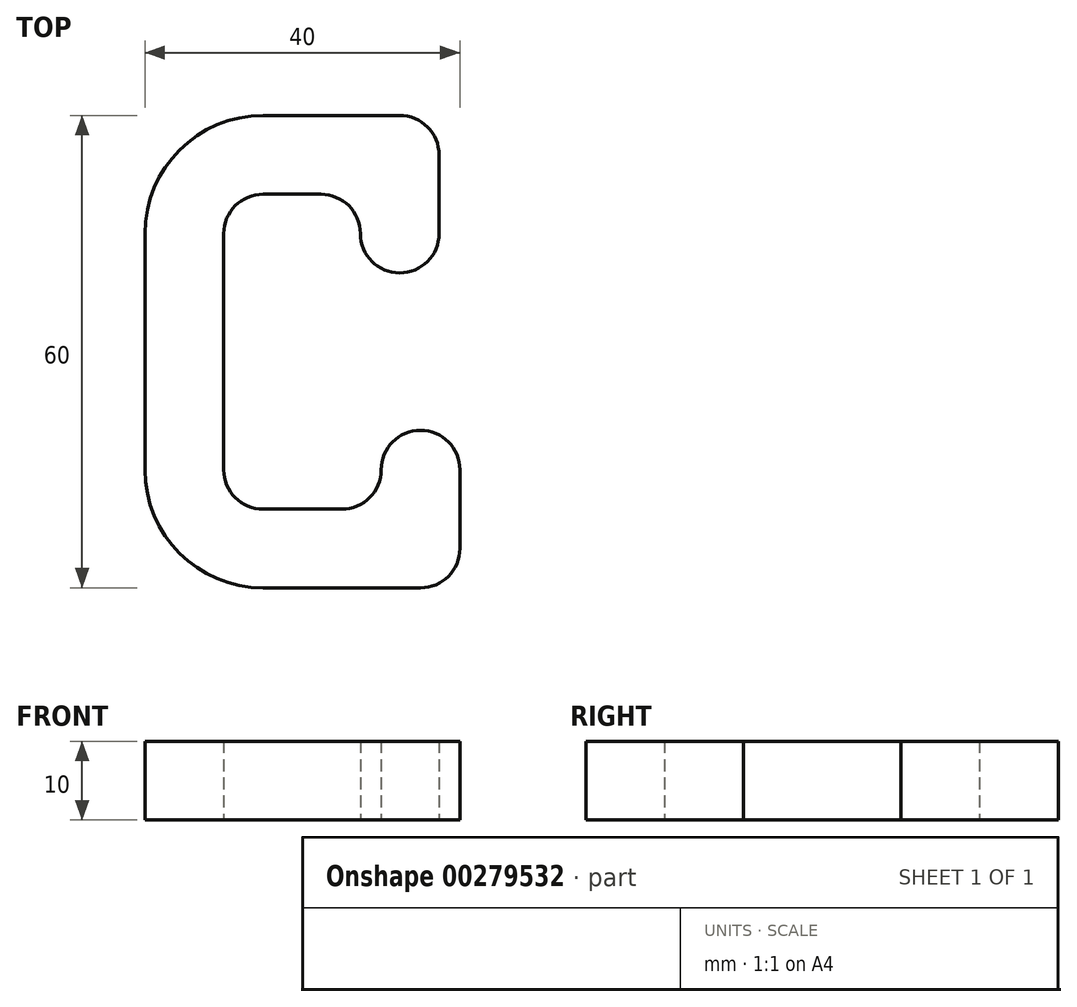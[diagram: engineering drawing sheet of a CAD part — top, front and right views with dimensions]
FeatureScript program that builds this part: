
annotation { "Feature Type Name" : "Feature", "Feature Type Description" : "" }
export const myFeature = defineFeature(function(context is Context, id is Id, definition is map)
    precondition{}
    {
        {
            var Q0;
            Q0=qCreatedBy(makeId("Top.planeOp"),FACE);
            var sketch = newSketch(context, id + "F0", { "sketchPlane" : qUnion([Q0])});
            skLineSegment(sketch, "E0.bottom", {"start": v(-16.46, 31.59) * mm, "end": v(-6.46, 31.59) * mm});
            skLineSegment(sketch, "E0.top", {"start": v(-16.46, -18.41) * mm, "end": v(-6.46, -18.41) * mm});
            skLineSegment(sketch, "E0.left", {"start": v(-16.46, 31.59) * mm, "end": v(-16.46, -18.41) * mm});
            skLineSegment(sketch, "E0.right", {"start": v(-6.46, 31.59) * mm, "end": v(-6.46, -18.41) * mm});
            skLineSegment(sketch, "E1.bottom", {"start": v(-16.46, 41.59) * mm, "end": v(10.9, 41.59) * mm});
            skLineSegment(sketch, "E1.top", {"start": v(-16.46, 31.59) * mm, "end": v(10.9, 31.59) * mm});
            skLineSegment(sketch, "E1.left", {"start": v(-16.46, 41.59) * mm, "end": v(-16.46, 31.59) * mm});
            skLineSegment(sketch, "E1.right", {"start": v(10.9, 41.59) * mm, "end": v(10.9, 31.59) * mm});
            skLineSegment(sketch, "E2.bottom", {"start": v(10.9, 41.59) * mm, "end": v(20.9, 41.59) * mm});
            skLineSegment(sketch, "E2.top", {"start": v(10.9, 21.59) * mm, "end": v(20.9, 21.59) * mm});
            skLineSegment(sketch, "E2.left", {"start": v(10.9, 41.59) * mm, "end": v(10.9, 21.59) * mm});
            skLineSegment(sketch, "E2.right", {"start": v(20.9, 41.59) * mm, "end": v(20.9, 21.59) * mm});
            skLineSegment(sketch, "E3.bottom", {"start": v(13.54, 1.59) * mm, "end": v(23.54, 1.59) * mm});
            skLineSegment(sketch, "E3.top", {"start": v(13.54, -8.41) * mm, "end": v(23.54, -8.41) * mm});
            skLineSegment(sketch, "E3.left", {"start": v(13.54, 1.59) * mm, "end": v(13.54, -8.41) * mm});
            skLineSegment(sketch, "E3.right", {"start": v(23.54, 1.59) * mm, "end": v(23.54, -8.41) * mm});
            skLineSegment(sketch, "E4.bottom", {"start": v(-6.46, -8.41) * mm, "end": v(23.54, -8.41) * mm});
            skLineSegment(sketch, "E4.top", {"start": v(-6.46, -18.41) * mm, "end": v(23.54, -18.41) * mm});
            skLineSegment(sketch, "E4.left", {"start": v(-6.46, -8.41) * mm, "end": v(-6.46, -18.41) * mm});
            skLineSegment(sketch, "E4.right", {"start": v(23.54, -8.41) * mm, "end": v(23.54, -18.41) * mm});
            skSolve(sketch);
        }
        {
            var Q0;
            {var subQ3=sQuery(id+"F0.wireOp",EDGE,"E2.bottom");Q0=makeQuery(id+"F0.imprint","IMPRINT",FACE,{"disambiguationData":[TD([[makeQuery(id+"F0.imprint","IMPRINT",EDGE,{"derivedFrom":subQ3}),-1.0]])]});}
            var Q1;
            {var subQ5=sQuery(id+"F0.wireOp",EDGE,"E1.bottom");Q1=makeQuery(id+"F0.imprint","IMPRINT",FACE,{"disambiguationData":[TD([[makeQuery(id+"F0.imprint","IMPRINT",EDGE,{"derivedFrom":subQ5}),-1.0]])]});}
            var Q2;
            Q2=makeQuery(id+"F0.imprint","IMPRINT",FACE,{"disambiguationData":[TD([[makeQuery(id+"F0.imprint","IMPRINT",EDGE,{"derivedFrom":sQuery(id+"F0.wireOp",EDGE,"E0.top")}),1.0]])]});
            var Q3;
            Q3=makeQuery(id+"F0.imprint","IMPRINT",FACE,{"disambiguationData":[TD([[makeQuery(id+"F0.imprint","IMPRINT",EDGE,{"derivedFrom":sQuery(id+"F0.wireOp",EDGE,"E4.top")}),1.0]])]});
            var Q4;
            Q4=makeQuery(id+"F0.imprint","IMPRINT",FACE,{"disambiguationData":[TD([[makeQuery(id+"F0.imprint","IMPRINT",EDGE,{"derivedFrom":sQuery(id+"F0.wireOp",EDGE,"E3.bottom")}),-1.0]])]});
            extrude(context, id + "F1", {"entities" : qUnion([Q0, Q1, Q2, Q3, Q4]), "depth" : 10 * mm});
        }
        {
            var Q0;
            Q0=makeQuery(id+"F1.opExtrude","SWEPT_EDGE",EDGE,{"disambiguationData":[OSD([sQuery(id+"F0.wireOp",EDGE,"E3.bottom"),sQuery(id+"F0.wireOp",EDGE,"E3.left")])]});
            var Q1;
            Q1=makeQuery(id+"F1.opExtrude","SWEPT_EDGE",EDGE,{"disambiguationData":[OSD([sQuery(id+"F0.wireOp",EDGE,"E2.top"),sQuery(id+"F0.wireOp",EDGE,"E2.left")])]});
            var Q2;
            Q2=makeQuery(id+"F1.opExtrude","SWEPT_EDGE",EDGE,{"disambiguationData":[OSD([sQuery(id+"F0.wireOp",EDGE,"E1.top"),sQuery(id+"F0.wireOp",EDGE,"E2.left")])]});
            var Q3;
            Q3=makeQuery(id+"F1.opExtrude","SWEPT_EDGE",EDGE,{"disambiguationData":[OSD([sQuery(id+"F0.wireOp",EDGE,"E0.right"),sQuery(id+"F0.wireOp",EDGE,"E1.top")])]});
            var Q4;
            Q4=makeQuery(id+"F1.opExtrude","SWEPT_EDGE",EDGE,{"disambiguationData":[OSD([sQuery(id+"F0.wireOp",EDGE,"E0.right"),sQuery(id+"F0.wireOp",EDGE,"E4.bottom"),sQuery(id+"F0.wireOp",EDGE,"E4.left")])]});
            var Q5;
            Q5=makeQuery(id+"F1.opExtrude","SWEPT_EDGE",EDGE,{"disambiguationData":[OSD([sQuery(id+"F0.wireOp",EDGE,"E3.left"),sQuery(id+"F0.wireOp",EDGE,"E4.bottom")])]});
            fillet(context, id + "F2", {"entities" : qUnion([Q0, Q1, Q2, Q3, Q4, Q5]), "radius" : 5 * mm, "tangentPropagation" : true, "allowEdgeOverflow" : false});
        }
        {
            var Q0;
            Q0=makeQuery(id+"F1.opExtrude","SWEPT_EDGE",EDGE,{"disambiguationData":[OSD([sQuery(id+"F0.wireOp",EDGE,"E3.bottom"),sQuery(id+"F0.wireOp",EDGE,"E3.right")])]});
            var Q1;
            Q1=makeQuery(id+"F1.opExtrude","SWEPT_EDGE",EDGE,{"disambiguationData":[OSD([sQuery(id+"F0.wireOp",EDGE,"E2.top"),sQuery(id+"F0.wireOp",EDGE,"E2.right")])]});
            fillet(context, id + "F3", {"entities" : qUnion([Q0, Q1]), "radius" : 5 * mm, "tangentPropagation" : true, "allowEdgeOverflow" : false});
        }
        {
            var Q0;
            Q0=makeQuery(id+"F1.opExtrude","SWEPT_EDGE",EDGE,{"disambiguationData":[OSD([sQuery(id+"F0.wireOp",EDGE,"E4.top"),sQuery(id+"F0.wireOp",EDGE,"E4.right")])]});
            var Q1;
            Q1=makeQuery(id+"F1.opExtrude","SWEPT_EDGE",EDGE,{"disambiguationData":[OSD([sQuery(id+"F0.wireOp",EDGE,"E2.bottom"),sQuery(id+"F0.wireOp",EDGE,"E2.right")])]});
            fillet(context, id + "F4", {"entities" : qUnion([Q0, Q1]), "radius" : 5 * mm, "tangentPropagation" : true, "allowEdgeOverflow" : false});
        }
        {
            var Q0;
            Q0=makeQuery(id+"F1.opExtrude","SWEPT_EDGE",EDGE,{"disambiguationData":[OSD([sQuery(id+"F0.wireOp",EDGE,"E0.top"),sQuery(id+"F0.wireOp",EDGE,"E0.left")])]});
            var Q1;
            Q1=makeQuery(id+"F1.opExtrude","SWEPT_EDGE",EDGE,{"disambiguationData":[OSD([sQuery(id+"F0.wireOp",EDGE,"E1.bottom"),sQuery(id+"F0.wireOp",EDGE,"E1.left")])]});
            fillet(context, id + "F5", {"entities" : qUnion([Q0, Q1]), "radius" : 15 * mm, "tangentPropagation" : true, "allowEdgeOverflow" : false});
        }
    });
